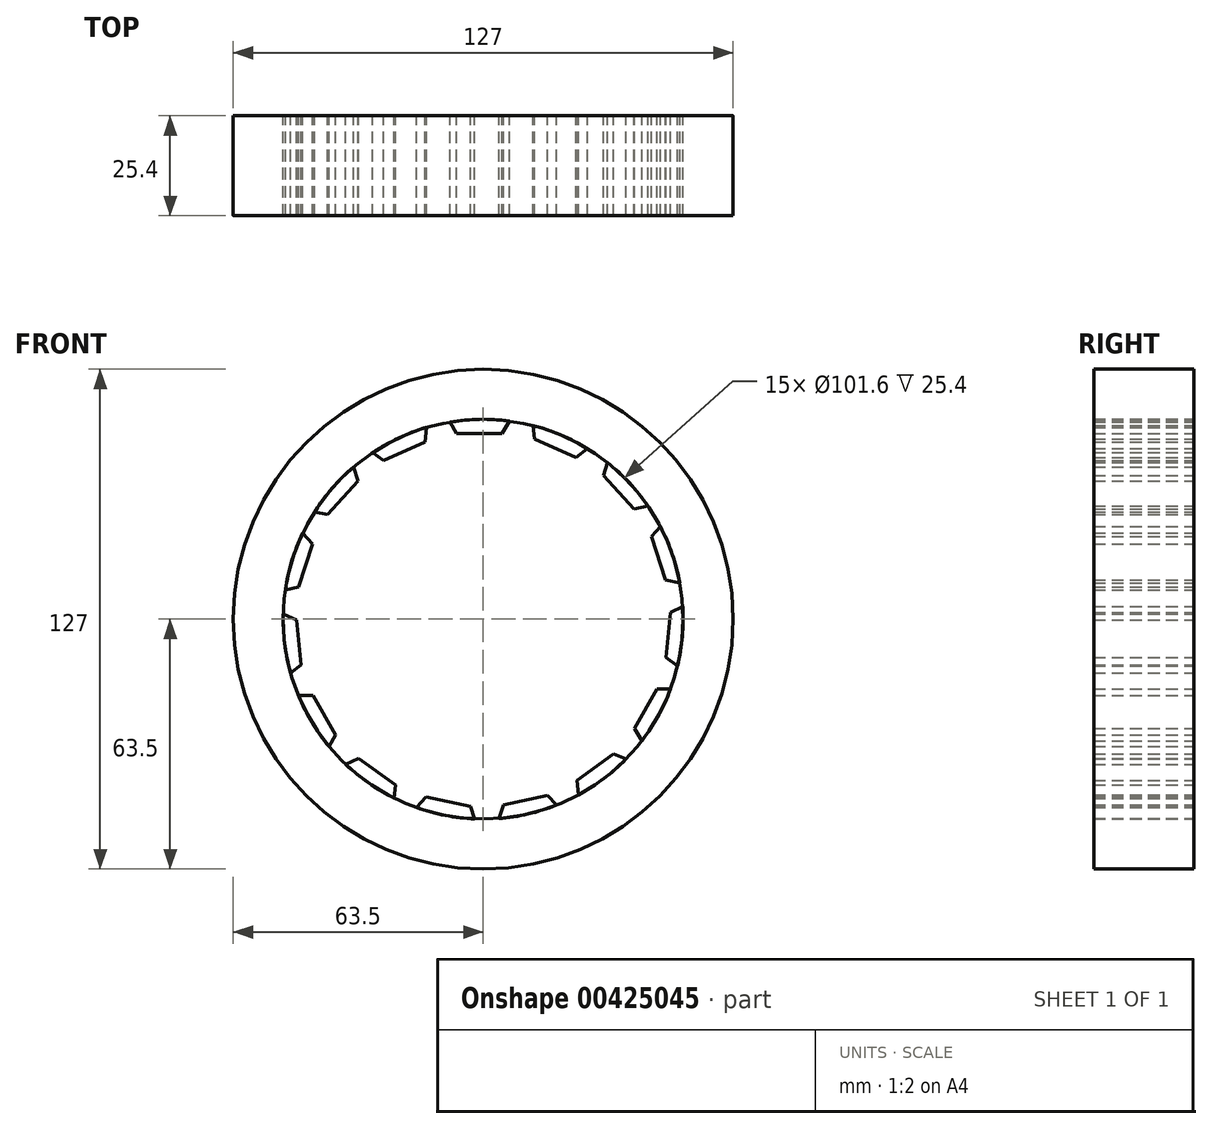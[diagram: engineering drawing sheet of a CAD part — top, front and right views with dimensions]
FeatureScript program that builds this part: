
annotation { "Feature Type Name" : "Feature", "Feature Type Description" : "" }
export const myFeature = defineFeature(function(context is Context, id is Id, definition is map)
    precondition{}
    {
        {
            var Q0;
            Q0=qCreatedBy(makeId("Front.planeOp"),FACE);
            var sketch = newSketch(context, id + "F0", { "sketchPlane" : qUnion([Q0])});
            skCircle(sketch, "E0", {"center": v(0, 0) * mm, "radius": 63.5 * mm});
            skCircle(sketch, "E1", {"center": v(0, 0) * mm, "radius": 50.8 * mm});
            skSolve(sketch);
        }
        {
            var Q0;
            Q0=makeQuery(id+"F0.imprint","IMPRINT",FACE,{"disambiguationData":[TD([[makeQuery(id+"F0.imprint","IMPRINT",EDGE,{"derivedFrom":sQuery(id+"F0.wireOp",EDGE,"E0")}),1.0]])]});
            extrude(context, id + "F1", {"entities" : qUnion([Q0]), "depth" : 25.4 * mm});
        }
        {
            var Q0;
            Q0=makeQuery(id+"F1.opExtrude","CAP_FACE",FACE,{"disambiguationData":[OSD([sQuery(id+"F0.wireOp",EDGE,"E0"),sQuery(id+"F0.wireOp",EDGE,"E1")])],"isStart":true});
            var sketch = newSketch(context, id + "F2", { "sketchPlane" : qUnion([Q0])});
            skLineSegment(sketch, "E2", {"start": v(-6.64, 50.36) * mm, "end": v(-4.8, 47.17) * mm});
            skLineSegment(sketch, "E3", {"start": v(-4.8, 47.17) * mm, "end": v(6.72, 47.17) * mm});
            skLineSegment(sketch, "E4", {"start": v(6.72, 47.17) * mm, "end": v(8.46, 50.1) * mm});
            skSolve(sketch);
        }
        {
            var Q0;
            {var subQ0=sQuery(id+"F2.wireOp",EDGE,"E2");Q0=makeQuery(id+"F2.imprint","IMPRINT",FACE,{"disambiguationData":[TD([[makeQuery(id+"F2.imprint","IMPRINT",EDGE,{"derivedFrom":subQ0}),1.0]])]});}
            extrude(context, id + "F3", {"entities" : qUnion([Q0]), "oppositeDirection" : true, "depth" : 25.4 * mm});
        }
        {
            var Q0;
            Q0=makeQuery(id+"F1.opExtrude","SWEPT_BODY",BODY,{"disambiguationData":[OSD([sQuery(id+"F0.wireOp",EDGE,"E0"),sQuery(id+"F0.wireOp",EDGE,"E1")])]});
            var Q1;
            Q1=makeQuery(id+"F3.opExtrude","SWEPT_BODY",BODY,{"disambiguationData":[OSD([sQuery(id+"F0.wireOp",EDGE,"E1"),sQuery(id+"F2.wireOp",EDGE,"E2"),sQuery(id+"F2.wireOp",EDGE,"E3"),sQuery(id+"F2.wireOp",EDGE,"E4")])]});
            var Q2;
            Q2=makeQuery(id+"F1.opExtrude","SWEPT_FACE",FACE,{"disambiguationData":[OSD([sQuery(id+"F0.wireOp",EDGE,"E1")])]});
            circularPattern(context, id + "F4", {"entities" : qUnion([Q0, Q1]), "axis" : qUnion([Q2]), "angle" : 360 * degree, "instanceCount" : 15, "equalSpace" : true});
        }
    });
